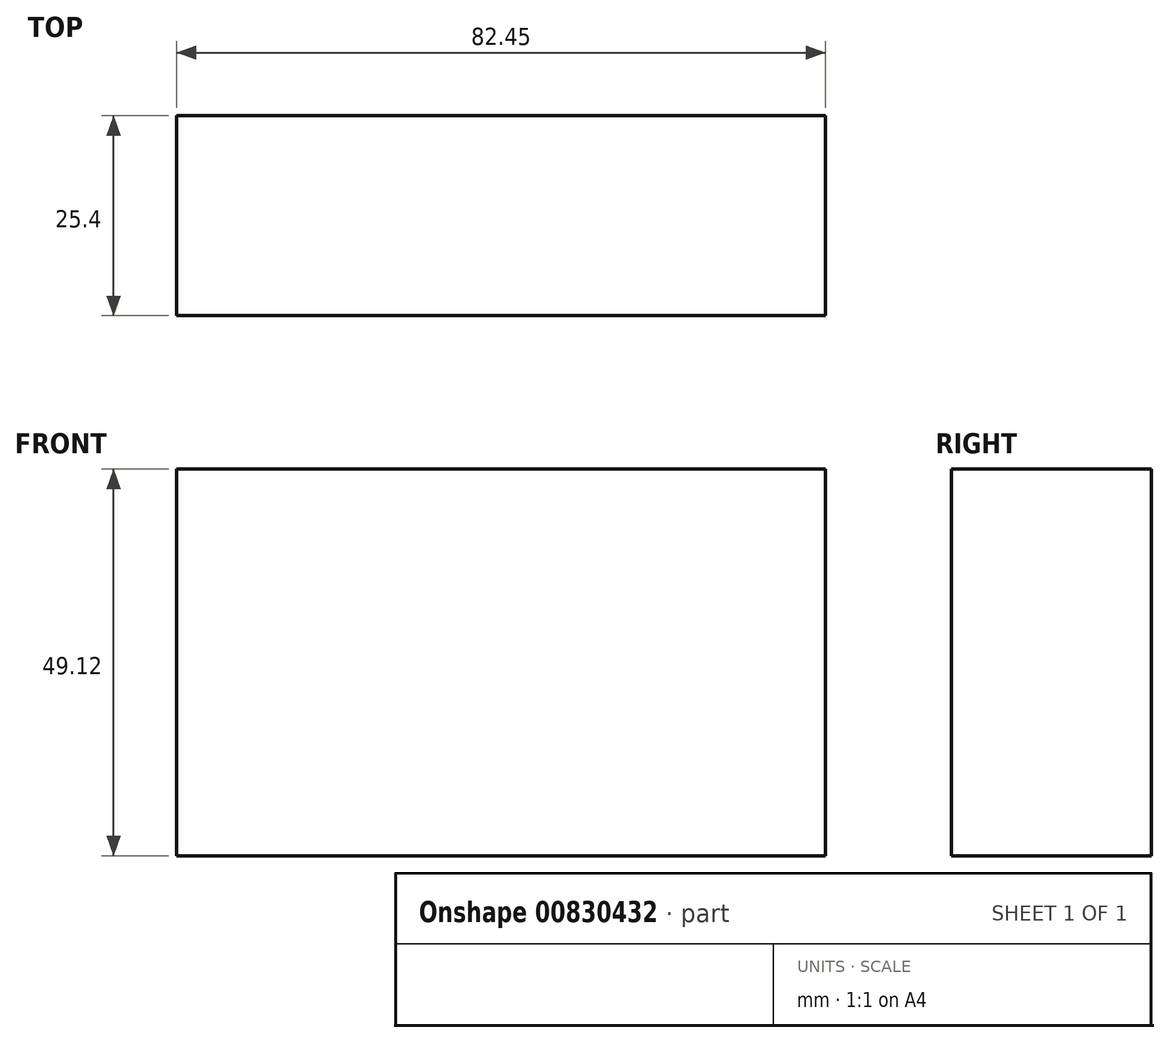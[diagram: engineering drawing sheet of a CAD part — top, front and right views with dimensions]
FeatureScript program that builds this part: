
annotation { "Feature Type Name" : "Feature", "Feature Type Description" : "" }
export const myFeature = defineFeature(function(context is Context, id is Id, definition is map)
    precondition{}
    {
        {
            var Q0;
            Q0=qCreatedBy(makeId("Front.planeOp"),FACE);
            var sketch = newSketch(context, id + "F0", { "sketchPlane" : qUnion([Q0])});
            skLineSegment(sketch, "E0.bottom", {"start": v(0, 49.12) * mm, "end": v(82.45, 49.12) * mm});
            skLineSegment(sketch, "E0.top", {"start": v(0, 0) * mm, "end": v(82.45, 0) * mm});
            skLineSegment(sketch, "E0.left", {"start": v(0, 49.12) * mm, "end": v(0, 0) * mm});
            skLineSegment(sketch, "E0.right", {"start": v(82.45, 49.12) * mm, "end": v(82.45, 0) * mm});
            skSolve(sketch);
        }
        {
            var Q0;
            Q0 = qSketchRegion(id + "F0", true);
            extrude(context, id + "F1", {"entities" : qUnion([Q0]), "depth" : 25.4 * mm, "offsetDistance" : 25.4 * mm});
        }
    });
